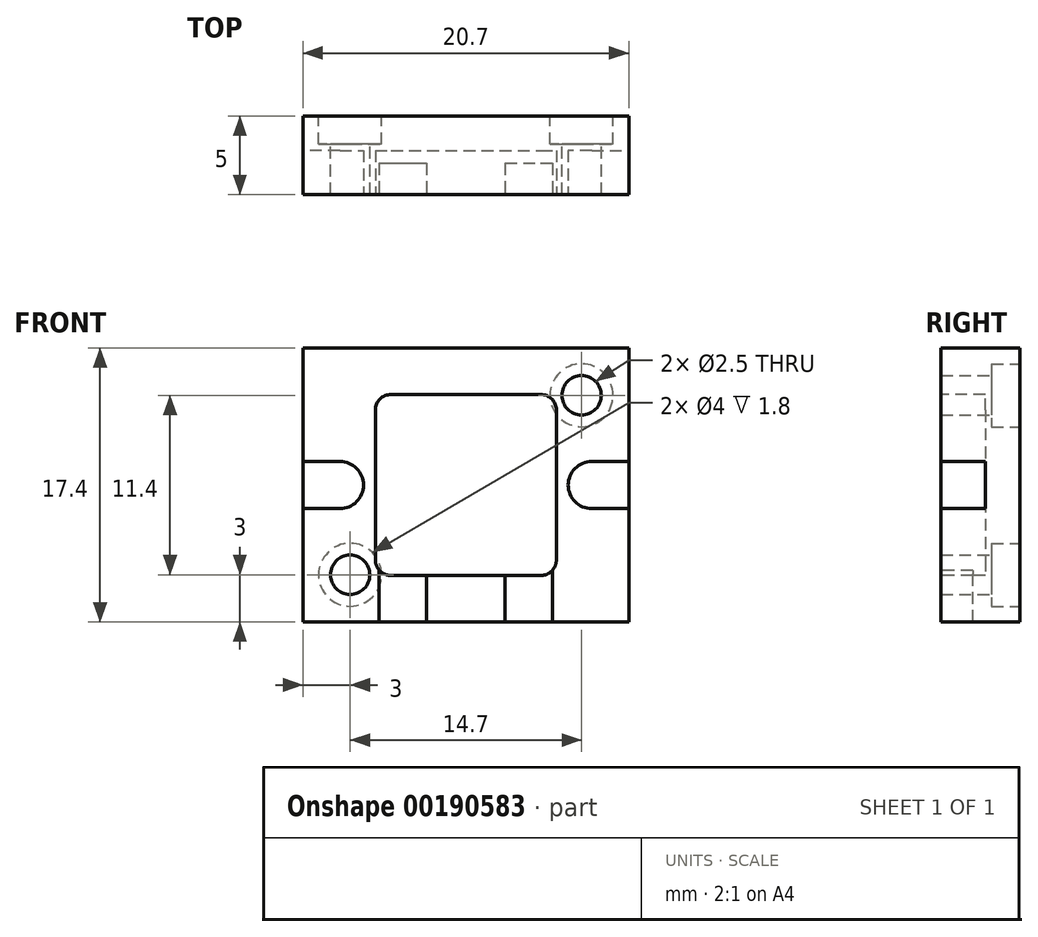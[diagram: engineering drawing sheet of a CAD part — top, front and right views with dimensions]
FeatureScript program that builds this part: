
annotation { "Feature Type Name" : "Feature", "Feature Type Description" : "" }
export const myFeature = defineFeature(function(context is Context, id is Id, definition is map)
    precondition{}
    {
        {
            var Q0;
            Q0=qCreatedBy(makeId("Front.planeOp"),FACE);
            var sketch = newSketch(context, id + "F0", { "sketchPlane" : qUnion([Q0])});
            skLineSegment(sketch, "E0.bottom", {"start": v(-10.35, 8.7) * mm, "end": v(10.35, 8.7) * mm});
            skLineSegment(sketch, "E0.top", {"start": v(-10.35, -8.7) * mm, "end": v(10.35, -8.7) * mm});
            skLineSegment(sketch, "E0.left", {"start": v(-10.35, 8.7) * mm, "end": v(-10.35, -8.7) * mm});
            skLineSegment(sketch, "E0.right", {"start": v(10.35, 8.7) * mm, "end": v(10.35, -8.7) * mm});
            skSolve(sketch);
        }
        {
            var Q0;
            Q0=makeQuery(id+"F0.imprint","IMPRINT",FACE,{"disambiguationData":[TD([[makeQuery(id+"F0.imprint","IMPRINT",EDGE,{"derivedFrom":sQuery(id+"F0.wireOp",EDGE,"E0.bottom")}),-1.0]])]});
            extrude(context, id + "F1", {"entities" : qUnion([Q0]), "oppositeDirection" : true, "depth" : 5 * mm});
        }
        {
            var Q0;
            Q0=makeQuery(id+"F1.opExtrude","CAP_FACE",FACE,{"disambiguationData":[OSD([sQuery(id+"F0.wireOp",EDGE,"E0.bottom"),sQuery(id+"F0.wireOp",EDGE,"E0.top"),sQuery(id+"F0.wireOp",EDGE,"E0.left"),sQuery(id+"F0.wireOp",EDGE,"E0.right")])],"isStart":true});
            var sketch = newSketch(context, id + "F2", { "sketchPlane" : qUnion([Q0])});
            skLineSegment(sketch, "E1.bottom", {"start": v(-5.75, 5.75) * mm, "end": v(5.75, 5.75) * mm});
            skLineSegment(sketch, "E1.top", {"start": v(-5.75, -5.75) * mm, "end": v(5.75, -5.75) * mm});
            skLineSegment(sketch, "E1.left", {"start": v(-5.75, 5.75) * mm, "end": v(-5.75, -5.75) * mm});
            skLineSegment(sketch, "E1.right", {"start": v(5.75, 5.75) * mm, "end": v(5.75, -5.75) * mm});
            skSolve(sketch);
        }
        {
            var Q0;
            Q0=makeQuery(id+"F2.imprint","IMPRINT",FACE,{"disambiguationData":[TD([[makeQuery(id+"F2.imprint","IMPRINT",EDGE,{"derivedFrom":sQuery(id+"F2.wireOp",EDGE,"E1.bottom")}),-1.0]])]});
            extrude(context, id + "F3", {"entities" : qUnion([Q0]), "operationType" : NewBodyOperationType.REMOVE, "oppositeDirection" : true, "depth" : 2.8 * mm});
        }
        {
            var Q0;
            Q0=makeQuery(id+"F1.opExtrude","CAP_FACE",FACE,{"disambiguationData":[OSD([sQuery(id+"F0.wireOp",EDGE,"E0.bottom"),sQuery(id+"F0.wireOp",EDGE,"E0.top"),sQuery(id+"F0.wireOp",EDGE,"E0.left"),sQuery(id+"F0.wireOp",EDGE,"E0.right")])],"isStart":true});
            var sketch = newSketch(context, id + "F4", { "sketchPlane" : qUnion([Q0])});
            skLineSegment(sketch, "E2.0", {"start": v(-8.35, 6.7) * mm, "end": v(-8.35, -6.7) * mm, "construction": true});
            skLineSegment(sketch, "E2.1", {"start": v(-8.35, 6.7) * mm, "end": v(8.35, 6.7) * mm, "construction": true});
            skLineSegment(sketch, "E2.2", {"start": v(8.35, 6.7) * mm, "end": v(8.35, -6.7) * mm, "construction": true});
            skLineSegment(sketch, "E2.3", {"start": v(-8.35, -6.7) * mm, "end": v(8.35, -6.7) * mm, "construction": true});
            skLineSegment(sketch, "E3", {"start": v(-8.35, 0) * mm, "end": v(8.35, 0) * mm, "construction": true});
            skSolve(sketch);
        }
        {
            var Q0;
            Q0=makeQuery(id+"F3.boolean.opBoolean","COPY",EDGE,{"derivedFrom":makeQuery(id+"F3.opExtrude","SWEPT_EDGE",EDGE,{"disambiguationData":[OSD([sQuery(id+"F2.wireOp",EDGE,"E1.bottom"),sQuery(id+"F2.wireOp",EDGE,"E1.left")])]})});
            var Q1;
            Q1=makeQuery(id+"F3.boolean.opBoolean","COPY",EDGE,{"derivedFrom":makeQuery(id+"F3.opExtrude","SWEPT_EDGE",EDGE,{"disambiguationData":[OSD([sQuery(id+"F2.wireOp",EDGE,"E1.bottom"),sQuery(id+"F2.wireOp",EDGE,"E1.right")])]})});
            var Q2;
            Q2=makeQuery(id+"F3.boolean.opBoolean","COPY",EDGE,{"derivedFrom":makeQuery(id+"F3.opExtrude","SWEPT_EDGE",EDGE,{"disambiguationData":[OSD([sQuery(id+"F2.wireOp",EDGE,"E1.top"),sQuery(id+"F2.wireOp",EDGE,"E1.left")])]})});
            var Q3;
            Q3=makeQuery(id+"F3.boolean.opBoolean","COPY",EDGE,{"derivedFrom":makeQuery(id+"F3.opExtrude","SWEPT_EDGE",EDGE,{"disambiguationData":[OSD([sQuery(id+"F2.wireOp",EDGE,"E1.top"),sQuery(id+"F2.wireOp",EDGE,"E1.right")])]})});
            fillet(context, id + "F5", {"entities" : qUnion([Q0, Q1, Q2, Q3]), "radius" : 1 * mm, "tangentPropagation" : true, "allowEdgeOverflow" : false});
        }
        {
            var Q0;
            Q0=makeQuery(id+"F1.opExtrude","CAP_FACE",FACE,{"disambiguationData":[OSD([sQuery(id+"F0.wireOp",EDGE,"E0.bottom"),sQuery(id+"F0.wireOp",EDGE,"E0.top"),sQuery(id+"F0.wireOp",EDGE,"E0.left"),sQuery(id+"F0.wireOp",EDGE,"E0.right")])],"isStart":true});
            var sketch = newSketch(context, id + "F6", { "sketchPlane" : qUnion([Q0])});
            skLineSegment(sketch, "E4.bottom", {"start": v(-5, 5) * mm, "end": v(5, 5) * mm, "construction": true});
            skLineSegment(sketch, "E4.top", {"start": v(-5, -5) * mm, "end": v(5, -5) * mm, "construction": true});
            skLineSegment(sketch, "E4.left", {"start": v(-5, 5) * mm, "end": v(-5, -5) * mm, "construction": true});
            skLineSegment(sketch, "E4.right", {"start": v(5, 5) * mm, "end": v(5, -5) * mm, "construction": true});
            skPoint(sketch, "E5.endSnap0", {"position": v(5.75, 0) * mm});
            skArc(sketch, "E6", {"start": v(-8, -1.5) * mm, "mid": v(-6.5, 0) * mm, "end": v(-8, 1.5) * mm});
            skArc(sketch, "E7", {"start": v(8, 1.5) * mm, "mid": v(6.5, 0) * mm, "end": v(8, -1.5) * mm});
            skLineSegment(sketch, "E8", {"start": v(-9.5, 0) * mm, "end": v(9.5, 0) * mm, "construction": true});
            skLineSegment(sketch, "E9", {"start": v(-8, 1.5) * mm, "end": v(-10.35, 1.5) * mm});
            skLineSegment(sketch, "E10", {"start": v(-8, -1.5) * mm, "end": v(-10.35, -1.5) * mm});
            skLineSegment(sketch, "E11", {"start": v(-10.35, -1.5) * mm, "end": v(-10.35, 1.5) * mm});
            skLineSegment(sketch, "E12", {"start": v(8, 0) * mm, "end": v(8, 1.5) * mm});
            skLineSegment(sketch, "E13", {"start": v(8, 1.5) * mm, "end": v(10.35, 1.5) * mm});
            skLineSegment(sketch, "E14", {"start": v(8, 0) * mm, "end": v(8, -1.5) * mm});
            skLineSegment(sketch, "E15", {"start": v(8, -1.5) * mm, "end": v(10.35, -1.5) * mm});
            skLineSegment(sketch, "E16", {"start": v(10.35, -1.5) * mm, "end": v(10.35, 1.5) * mm});
            skSolve(sketch);
        }
        {
            var Q0;
            Q0=makeQuery(id+"F6.imprint","IMPRINT",FACE,{"disambiguationData":[TD([[makeQuery(id+"F6.imprint","IMPRINT",EDGE,{"derivedFrom":sQuery(id+"F6.wireOp",EDGE,"E6")}),1.0]])]});
            var Q1;
            Q1=makeQuery(id+"F6.imprint","IMPRINT",FACE,{"disambiguationData":[TD([[makeQuery(id+"F6.imprint","IMPRINT",EDGE,{"derivedFrom":sQuery(id+"F6.wireOp",EDGE,"E7")}),1.0]])]});
            var Q2;
            Q2=makeQuery(id+"F6.imprint","IMPRINT",FACE,{"disambiguationData":[TD([[makeQuery(id+"F6.imprint","IMPRINT",EDGE,{"derivedFrom":sQuery(id+"F6.wireOp",EDGE,"E12")}),-1.0]])]});
            extrude(context, id + "F7", {"entities" : qUnion([Q0, Q1, Q2]), "operationType" : NewBodyOperationType.REMOVE, "oppositeDirection" : true, "depth" : 2.8 * mm});
        }
        {
            var Q0;
            Q0=makeQuery(id+"F1.opExtrude","CAP_FACE",FACE,{"disambiguationData":[OSD([sQuery(id+"F0.wireOp",EDGE,"E0.bottom"),sQuery(id+"F0.wireOp",EDGE,"E0.top"),sQuery(id+"F0.wireOp",EDGE,"E0.left"),sQuery(id+"F0.wireOp",EDGE,"E0.right")])],"isStart":false});
            var sketch = newSketch(context, id + "F8", { "sketchPlane" : qUnion([Q0])});
            skLineSegment(sketch, "E17.0", {"start": v(-7.35, 5.7) * mm, "end": v(-7.35, -5.7) * mm, "construction": true});
            skLineSegment(sketch, "E17.1", {"start": v(7.35, 5.7) * mm, "end": v(-7.35, 5.7) * mm, "construction": true});
            skLineSegment(sketch, "E17.2", {"start": v(7.35, 5.7) * mm, "end": v(7.35, -5.7) * mm, "construction": true});
            skLineSegment(sketch, "E17.3", {"start": v(7.35, -5.7) * mm, "end": v(-7.35, -5.7) * mm, "construction": true});
            skSolve(sketch);
        }
        {
            var Q0;
            Q0=sQuery(id+"F8.wireOp",VERTEX,"E17.3.start");
            var Q1;
            Q1=sQuery(id+"F8.wireOp",VERTEX,"E17.0.start");
            var Q2;
            Q2=makeQuery(id+"F1.opExtrude","SWEPT_BODY",BODY,{"disambiguationData":[OSD([sQuery(id+"F0.wireOp",EDGE,"E0.bottom"),sQuery(id+"F0.wireOp",EDGE,"E0.top"),sQuery(id+"F0.wireOp",EDGE,"E0.left"),sQuery(id+"F0.wireOp",EDGE,"E0.right")])]});
            hole(context, id + "F9", {"style" : HoleStyle.C_BORE, "endStyle" : HoleEndStyle.BLIND, "holeDiameter" : 2.5 * mm, "cBoreDiameter" : 4 * mm, "cBoreDepth" : 1.8 * mm, "holeDepth" : 5 * mm, "locations" : qUnion([Q0, Q1]), "scope" : qUnion([Q2])});
        }
        {
            var Q0;
            Q0=makeQuery(id+"F6.imprint","IMPRINT",FACE,{"disambiguationData":[TD([[makeQuery(id+"F6.imprint","IMPRINT",EDGE,{"derivedFrom":sQuery(id+"F6.wireOp",EDGE,"E6")}),-1.0]])]});
            var sketch = newSketch(context, id + "F10", { "sketchPlane" : qUnion([Q0])});
            skArc(sketch, "E18.0", {"start": v(4.75, 5.75) * mm, "mid": v(5.46, 5.46) * mm, "end": v(5.75, 4.75) * mm, "construction": true});
            skLineSegment(sketch, "E19.0", {"start": v(-4.75, -5.75) * mm, "end": v(4.75, -5.75) * mm});
            skArc(sketch, "E20.0", {"start": v(-4.75, -5.75) * mm, "mid": v(-5.46, -5.46) * mm, "end": v(-5.75, -4.75) * mm});
            skLineSegment(sketch, "E21", {"start": v(-5.5, -8.7) * mm, "end": v(-5.5, -5.41) * mm});
            skLineSegment(sketch, "E22", {"start": v(-2.5, -8.7) * mm, "end": v(-2.5, -5.75) * mm});
            skLineSegment(sketch, "E23", {"start": v(0, 0) * mm, "end": v(0, -5.75) * mm, "construction": true});
            skLineSegment(sketch, "E24.MirrorCS", {"start": v(2.5, -8.7) * mm, "end": v(2.5, -5.75) * mm});
            skLineSegment(sketch, "E25.MirrorCS", {"start": v(5.5, -8.7) * mm, "end": v(5.5, -5.41) * mm});
            skLineSegment(sketch, "E26.MirrorCS", {"start": v(4.75, -5.75) * mm, "end": v(-4.75, -5.75) * mm});
            skArc(sketch, "E27.MirrorCS", {"start": v(4.75, -5.75) * mm, "mid": v(5.46, -5.46) * mm, "end": v(5.75, -4.75) * mm});
            skLineSegment(sketch, "E28.0", {"start": v(-10.35, -8.7) * mm, "end": v(10.35, -8.7) * mm});
            skPoint(sketch, "E29.orphan", {"position": v(-5.5, -7.25) * mm});
            skPoint(sketch, "E30.orphan", {"position": v(-2.5, -7.25) * mm});
            skPoint(sketch, "E31.orphan", {"position": v(2.5, -7.25) * mm});
            skPoint(sketch, "E32.orphan", {"position": v(5.5, -7.25) * mm});
            skPoint(sketch, "E33.orphan", {"position": v(-5.5, -4.09) * mm});
            skPoint(sketch, "E34.orphan", {"position": v(5.5, -4.09) * mm});
            skSolve(sketch);
        }
        {
            var Q0;
            Q0=makeQuery(id+"F10.imprint","IMPRINT",FACE,{"disambiguationData":[TD([[makeQuery(id+"F10.imprint","IMPRINT",EDGE,{"derivedFrom":sQuery(id+"F10.wireOp",EDGE,"abPfINNU-Qiff-eJsQ-xV5Q-1ainPu6RhAzz")}),1.0]])]});
            var Q1;
            {var subQ4=sQuery(id+"F10.wireOp",EDGE,"E24.MirrorCS");Q1=makeQuery(id+"F10.imprint","IMPRINT",FACE,{"disambiguationData":[TD([[makeQuery(id+"F10.imprint","IMPRINT",EDGE,{"derivedFrom":subQ4}),-1.0]])]});}
            var Q2;
            {var subQ5=sQuery(id+"F10.wireOp",EDGE,"E21");Q2=makeQuery(id+"F10.imprint","IMPRINT",FACE,{"disambiguationData":[TD([[makeQuery(id+"F10.imprint","IMPRINT",EDGE,{"derivedFrom":subQ5}),-1.0]])]});}
            extrude(context, id + "F11", {"entities" : qUnion([Q0, Q1, Q2]), "operationType" : NewBodyOperationType.REMOVE, "oppositeDirection" : true, "depth" : 2 * mm});
        }
    });
